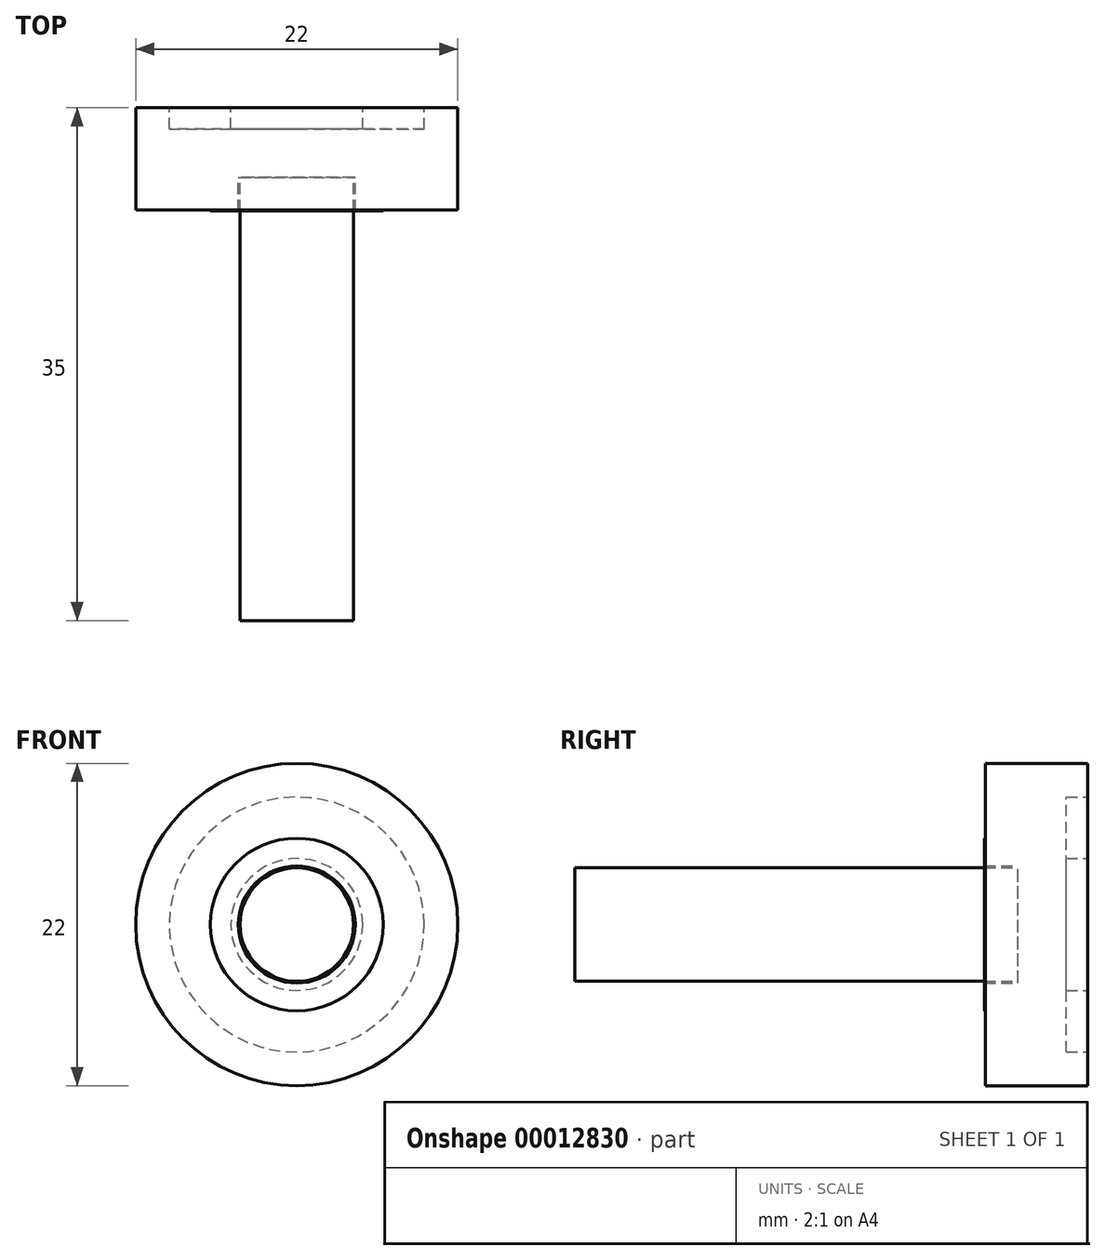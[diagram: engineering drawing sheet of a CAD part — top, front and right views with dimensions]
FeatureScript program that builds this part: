
annotation { "Feature Type Name" : "Feature", "Feature Type Description" : "" }
export const myFeature = defineFeature(function(context is Context, id is Id, definition is map)
    precondition{}
    {
        {
            var Q0;
            Q0=qCreatedBy(makeId("Front.planeOp"),FACE);
            var sketch = newSketch(context, id + "F0", { "sketchPlane" : qUnion([Q0])});
            skCircle(sketch, "E0", {"center": v(0, 0) * mm, "radius": 11 * mm});
            skCircle(sketch, "E1", {"center": v(0, 0) * mm, "radius": 4 * mm});
            skCircle(sketch, "E2.0", {"center": v(0, 0) * mm, "radius": 5.9 * mm});
            skSolve(sketch);
        }
        {
            var Q0;
            Q0=makeQuery(id+"F0.imprint","IMPRINT",FACE,{"disambiguationData":[TD([[makeQuery(id+"F0.imprint","IMPRINT",EDGE,{"derivedFrom":sQuery(id+"F0.wireOp",EDGE,"E0")}),1.0]])]});
            extrude(context, id + "F1", {"entities" : qUnion([Q0]), "depth" : 6.97 * mm});
        }
        {
            var Q0;
            Q0=makeQuery(id+"F0.imprint","IMPRINT",FACE,{"disambiguationData":[TD([[makeQuery(id+"F0.imprint","IMPRINT",EDGE,{"derivedFrom":sQuery(id+"F0.wireOp",EDGE,"E1")}),-1.0]])]});
            extrude(context, id + "F2", {"entities" : qUnion([Q0]), "depth" : 7.04 * mm});
        }
        {
            var Q0;
            Q0=qCreatedBy(makeId("Front.planeOp"),FACE);
            var sketch = newSketch(context, id + "F3", { "sketchPlane" : qUnion([Q0])});
            skCircle(sketch, "E3.cCircle", {"center": v(0, 0) * mm, "radius": 6.88 * mm, "construction": true});
            skLineSegment(sketch, "E3.0", {"start": v(7.75, 1.73) * mm, "end": v(5.37, -5.84) * mm});
            skLineSegment(sketch, "E3.1", {"start": v(5.37, -5.84) * mm, "end": v(-2.38, -7.57) * mm});
            skLineSegment(sketch, "E3.2", {"start": v(-2.38, -7.57) * mm, "end": v(-7.75, -1.73) * mm});
            skLineSegment(sketch, "E3.3", {"start": v(-7.75, -1.73) * mm, "end": v(-5.37, 5.84) * mm});
            skLineSegment(sketch, "E3.4", {"start": v(-5.37, 5.84) * mm, "end": v(2.38, 7.57) * mm});
            skLineSegment(sketch, "E3.5", {"start": v(2.38, 7.57) * mm, "end": v(7.75, 1.73) * mm});
            skPoint(sketch, "E3.0.midPoint", {"position": v(6.56, -2.06) * mm});
            skCircle(sketch, "E4", {"center": v(0, 0) * mm, "radius": 3.88 * mm});
            skSolve(sketch);
        }
        {
            var Q0;
            Q0=makeQuery(id+"F3.imprint","IMPRINT",FACE,{"disambiguationData":[TD([[makeQuery(id+"F3.imprint","IMPRINT",EDGE,{"derivedFrom":sQuery(id+"F3.wireOp",EDGE,"E4")}),1.0]])]});
            extrude(context, id + "F4", {"entities" : qUnion([Q0]), "depth" : 35 * mm});
        }
        {
            var Q0;
            Q0 = qSketchRegion(id + "F3", true);
            extrude(context, id + "F5", {"entities" : qUnion([Q0]), "operationType" : NewBodyOperationType.ADD, "depth" : 4.75 * mm});
        }
        {
            var Q0;
            Q0=qCreatedBy(makeId("Front.planeOp"),FACE);
            var sketch = newSketch(context, id + "F6", { "sketchPlane" : qUnion([Q0])});
            skCircle(sketch, "E5", {"center": v(0, 0) * mm, "radius": 8.7 * mm});
            skCircle(sketch, "E6", {"center": v(0, 0) * mm, "radius": 4.5 * mm});
            skSolve(sketch);
        }
        {
            var Q0;
            Q0 = qSketchRegion(id + "F6", true);
            extrude(context, id + "F7", {"entities" : qUnion([Q0]), "depth" : 1.45 * mm});
        }
    });
